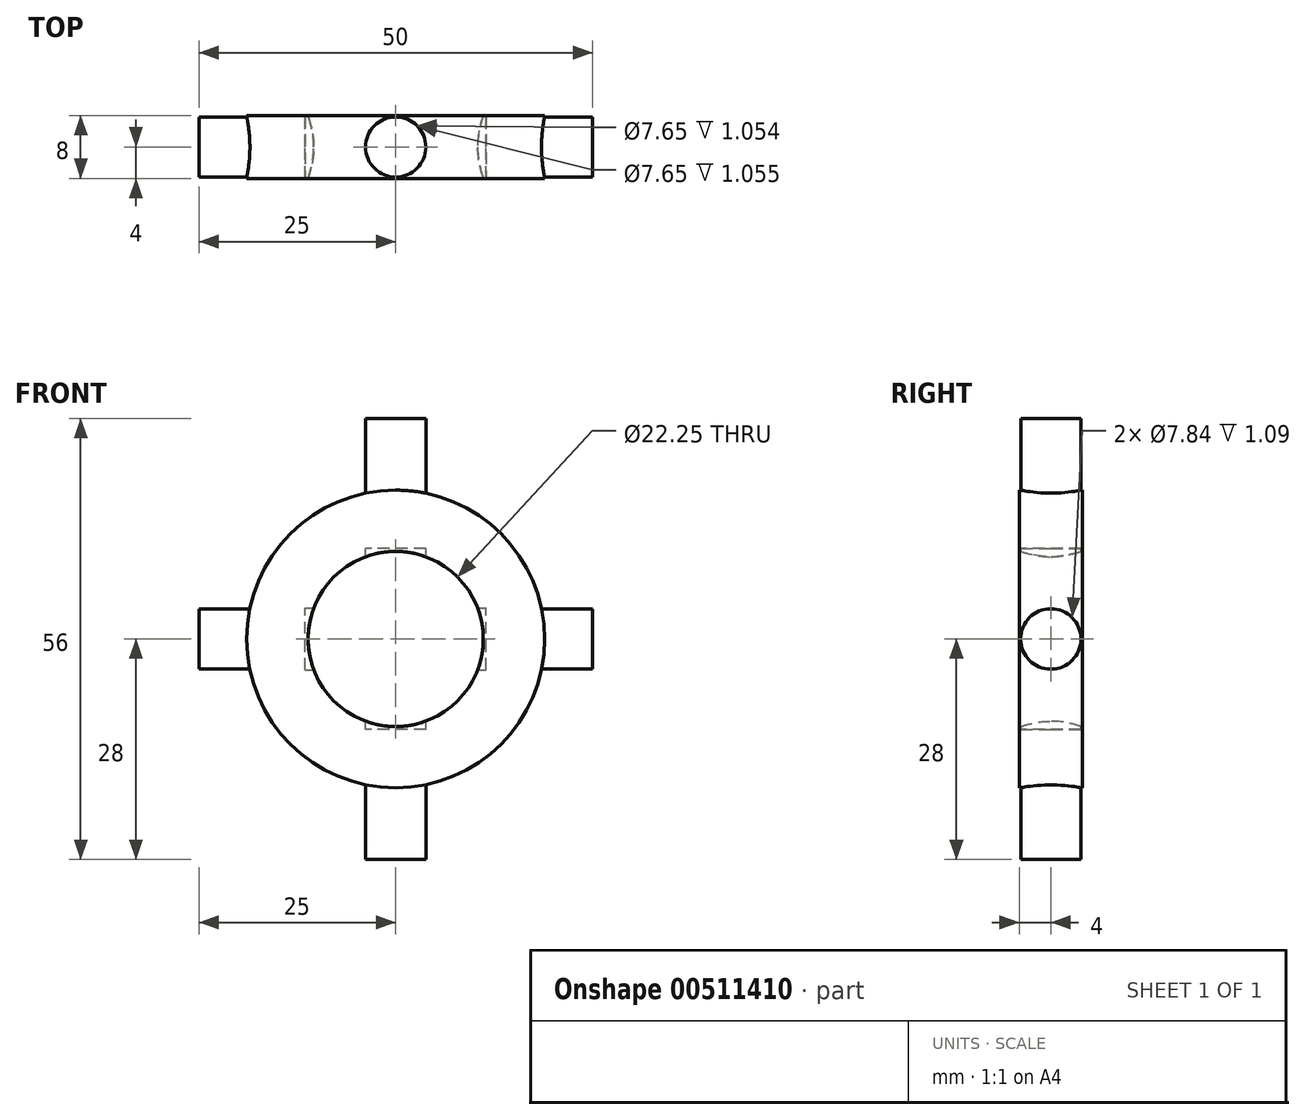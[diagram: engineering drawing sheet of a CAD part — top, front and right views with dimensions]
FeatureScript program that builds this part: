
annotation { "Feature Type Name" : "Feature", "Feature Type Description" : "" }
export const myFeature = defineFeature(function(context is Context, id is Id, definition is map)
    precondition{}
    {
        {
            var Q0;
            Q0=qCreatedBy(makeId("Front.planeOp"),FACE);
            var sketch = newSketch(context, id + "F0", { "sketchPlane" : qUnion([Q0])});
            skCircle(sketch, "E0", {"center": v(0, 0) * mm, "radius": 11.13 * mm});
            skCircle(sketch, "E1", {"center": v(0, 0) * mm, "radius": 18.91 * mm});
            skSolve(sketch);
        }
        {
            var Q0;
            Q0=makeQuery(id+"F0.imprint","IMPRINT",FACE,{"disambiguationData":[TD([[makeQuery(id+"F0.imprint","IMPRINT",EDGE,{"derivedFrom":sQuery(id+"F0.wireOp",EDGE,"E0")}),-1.0]])]});
            extrude(context, id + "F1", {"entities" : qUnion([Q0]), "depth" : 4 * mm, "hasSecondDirection" : true, "secondDirectionOppositeDirection" : true, "secondDirectionDepth" : 4 * mm});
        }
        {
            var Q0;
            Q0=qCreatedBy(makeId("Top.planeOp"),FACE);
            var sketch = newSketch(context, id + "F2", { "sketchPlane" : qUnion([Q0])});
            skLineSegment(sketch, "E2", {"start": v(-4, 18.91) * mm, "end": v(4, 18.91) * mm});
            skCircle(sketch, "E3", {"center": v(0, 0) * mm, "radius": 3.83 * mm});
            skCircle(sketch, "E4", {"center": v(-28.37, -16.38) * mm, "radius": 3.88 * mm});
            skSolve(sketch);
        }
        {
            var Q0;
            Q0=makeQuery(id+"F2.imprint","IMPRINT",FACE,{"disambiguationData":[TD([[makeQuery(id+"F2.imprint","IMPRINT",EDGE,{"derivedFrom":sQuery(id+"F2.wireOp",EDGE,"E3")}),1.0]])]});
            extrude(context, id + "F3", {"entities" : qUnion([Q0]), "operationType" : NewBodyOperationType.ADD, "depth" : 28 * mm, "hasSecondDirection" : true, "secondDirectionOppositeDirection" : true, "secondDirectionDepth" : 28 * mm});
        }
        {
            var Q0;
            Q0=qCreatedBy(makeId("Top.planeOp"),FACE);
            var sketch = newSketch(context, id + "F4", { "sketchPlane" : qUnion([Q0])});
            skCircle(sketch, "E5", {"center": v(0, 0) * mm, "radius": 3.83 * mm});
            skSolve(sketch);
        }
        {
            var Q0;
            Q0=makeQuery(id+"F4.imprint","IMPRINT",FACE,{"disambiguationData":[TD([[makeQuery(id+"F4.imprint","IMPRINT",EDGE,{"derivedFrom":sQuery(id+"F4.wireOp",EDGE,"E5")}),1.0]])]});
            extrude(context, id + "F5", {"entities" : qUnion([Q0]), "operationType" : NewBodyOperationType.REMOVE, "oppositeDirection" : true, "depth" : 11.5 * mm, "hasSecondDirection" : true, "secondDirectionOppositeDirection" : false, "secondDirectionDepth" : 11.5 * mm});
        }
        {
            var Q0;
            Q0=qCreatedBy(makeId("Right.planeOp"),FACE);
            var sketch = newSketch(context, id + "F6", { "sketchPlane" : qUnion([Q0])});
            skCircle(sketch, "E6", {"center": v(0, 0) * mm, "radius": 3.83 * mm});
            skSolve(sketch);
        }
        {
            var Q0;
            Q0=makeQuery(id+"F6.imprint","IMPRINT",FACE,{"disambiguationData":[TD([[makeQuery(id+"F6.imprint","IMPRINT",EDGE,{"derivedFrom":sQuery(id+"F6.wireOp",EDGE,"E6")}),1.0]])]});
            extrude(context, id + "F7", {"entities" : qUnion([Q0]), "operationType" : NewBodyOperationType.ADD, "depth" : 25 * mm, "hasSecondDirection" : true, "secondDirectionOppositeDirection" : true, "secondDirectionDepth" : 25 * mm});
        }
        {
            var Q0;
            Q0=qCreatedBy(makeId("Right.planeOp"),FACE);
            var sketch = newSketch(context, id + "F8", { "sketchPlane" : qUnion([Q0])});
            skCircle(sketch, "E7", {"center": v(0, 0) * mm, "radius": 3.92 * mm});
            skSolve(sketch);
        }
        {
            var Q0;
            Q0=makeQuery(id+"F8.imprint","IMPRINT",FACE,{"disambiguationData":[TD([[makeQuery(id+"F8.imprint","IMPRINT",EDGE,{"derivedFrom":sQuery(id+"F8.wireOp",EDGE,"E7")}),1.0]])]});
            extrude(context, id + "F9", {"entities" : qUnion([Q0]), "operationType" : NewBodyOperationType.REMOVE, "oppositeDirection" : true, "depth" : 11.5 * mm, "hasSecondDirection" : true, "secondDirectionOppositeDirection" : false, "secondDirectionDepth" : 11.5 * mm});
        }
    });
